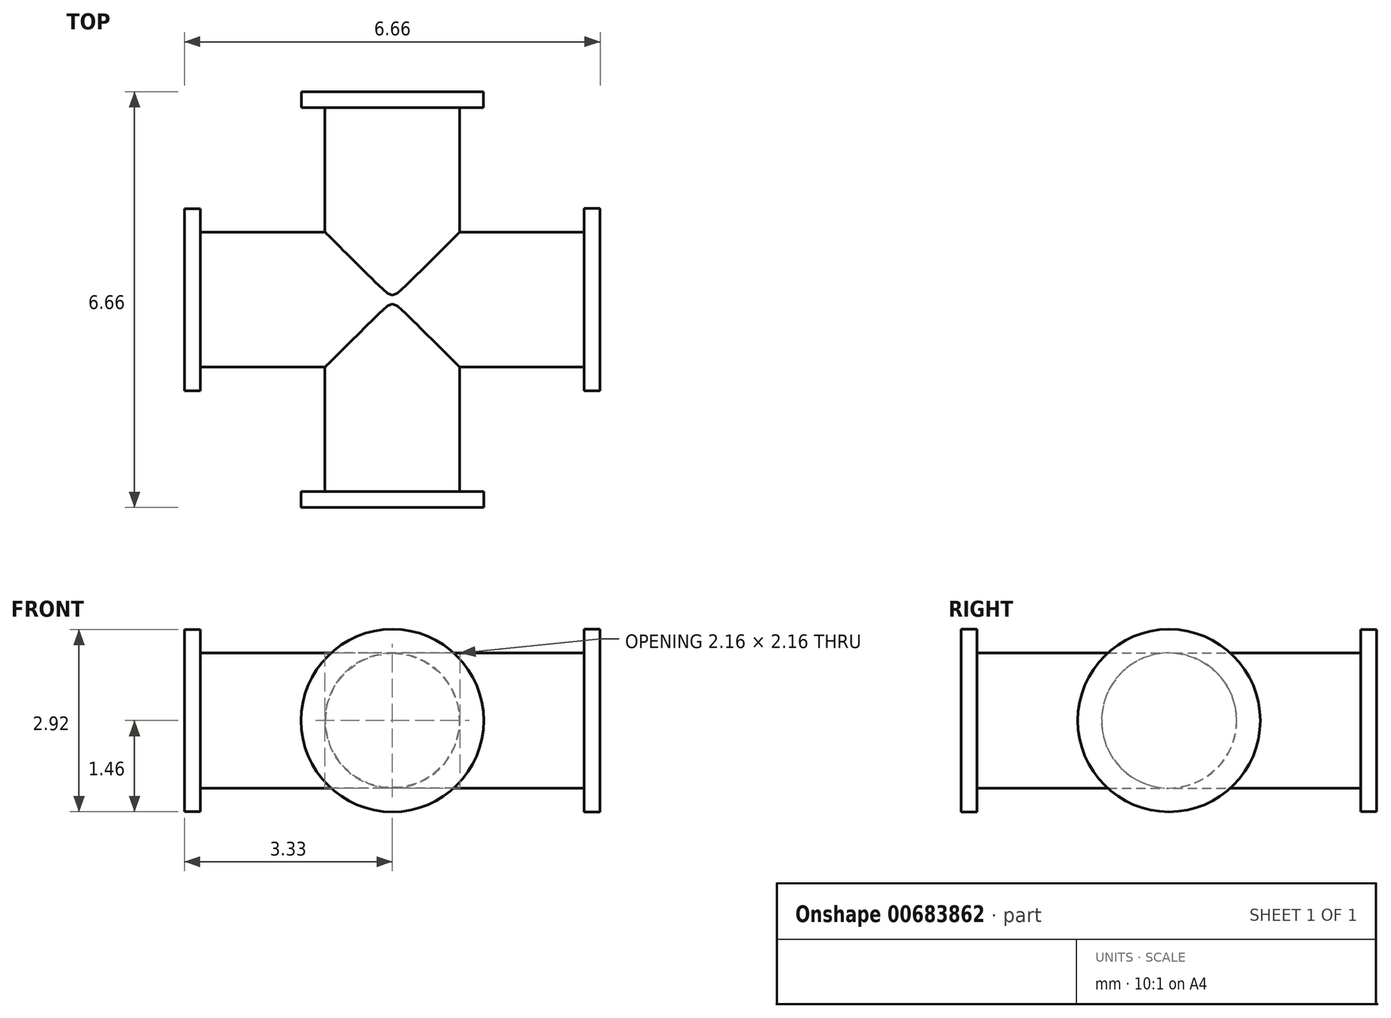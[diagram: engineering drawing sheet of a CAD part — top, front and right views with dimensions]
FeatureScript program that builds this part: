
annotation { "Feature Type Name" : "Feature", "Feature Type Description" : "" }
export const myFeature = defineFeature(function(context is Context, id is Id, definition is map)
    precondition{}
    {
        {
            var Q0;
            Q0=qCreatedBy(makeId("Front.planeOp"),FACE);
            var sketch = newSketch(context, id + "F0", { "sketchPlane" : qUnion([Q0])});
            skCircle(sketch, "E0", {"center": v(0, 0) * mm, "radius": 1.08 * mm});
            skSolve(sketch);
        }
        {
            var Q0;
            Q0=makeQuery(id+"F0.imprint","IMPRINT",FACE,{"disambiguationData":[TD([[makeQuery(id+"F0.imprint","IMPRINT",EDGE,{"derivedFrom":sQuery(id+"F0.wireOp",EDGE,"E0")}),1.0]])]});
            extrude(context, id + "F1", {"entities" : qUnion([Q0]), "depth" : 3.07 * mm, "offsetDistance" : 25.4 * mm, "hasSecondDirection" : true, "secondDirectionOppositeDirection" : true, "secondDirectionDepth" : 3.07 * mm});
        }
        {
            var Q0;
            Q0=qCreatedBy(makeId("Right.planeOp"),FACE);
            var sketch = newSketch(context, id + "F2", { "sketchPlane" : qUnion([Q0])});
            skCircle(sketch, "E1", {"center": v(0, 0) * mm, "radius": 1.08 * mm});
            skSolve(sketch);
        }
        {
            var Q0;
            Q0 = qSketchRegion(id + "F2", true);
            extrude(context, id + "F3", {"entities" : qUnion([Q0]), "operationType" : NewBodyOperationType.ADD, "depth" : 3.07 * mm, "offsetDistance" : 25.4 * mm, "hasSecondDirection" : true, "secondDirectionOppositeDirection" : true, "secondDirectionDepth" : 3.07 * mm});
        }
        {
            var Q0;
            Q0=makeQuery(id+"F1.opExtrude","CAP_FACE",FACE,{"disambiguationData":[OSD([sQuery(id+"F0.wireOp",EDGE,"E0")])],"isStart":false});
            var sketch = newSketch(context, id + "F4", { "sketchPlane" : qUnion([Q0])});
            skCircle(sketch, "E2", {"center": v(0, 0) * mm, "radius": 1.46 * mm});
            skSolve(sketch);
        }
        {
            var Q0;
            Q0 = qSketchRegion(id + "F4", true);
            extrude(context, id + "F5", {"entities" : qUnion([Q0]), "operationType" : NewBodyOperationType.ADD, "depth" : 0.25 * mm, "offsetDistance" : 25.4 * mm});
        }
        {
            var Q0;
            Q0=makeQuery(id+"F3.opExtrude","CAP_FACE",FACE,{"disambiguationData":[OSD([sQuery(id+"F2.wireOp",EDGE,"E1")])],"isStart":false});
            var sketch = newSketch(context, id + "F6", { "sketchPlane" : qUnion([Q0])});
            skCircle(sketch, "E3", {"center": v(0, 0) * mm, "radius": 1.46 * mm});
            skSolve(sketch);
        }
        {
            var Q0;
            Q0 = qSketchRegion(id + "F6", true);
            extrude(context, id + "F7", {"entities" : qUnion([Q0]), "operationType" : NewBodyOperationType.ADD, "depth" : 0.25 * mm, "offsetDistance" : 25.4 * mm});
        }
        {
            var Q0;
            Q0=makeQuery(id+"F1.opExtrude","CAP_FACE",FACE,{"disambiguationData":[OSD([sQuery(id+"F0.wireOp",EDGE,"E0")])],"isStart":true});
            var sketch = newSketch(context, id + "F8", { "sketchPlane" : qUnion([Q0])});
            skCircle(sketch, "E4", {"center": v(0, 0) * mm, "radius": 1.46 * mm});
            skSolve(sketch);
        }
        {
            var Q0;
            Q0 = qSketchRegion(id + "F8", true);
            extrude(context, id + "F9", {"entities" : qUnion([Q0]), "operationType" : NewBodyOperationType.ADD, "depth" : 0.25 * mm, "offsetDistance" : 25.4 * mm});
        }
        {
            var Q0;
            Q0=makeQuery(id+"F3.opExtrude","CAP_FACE",FACE,{"disambiguationData":[OSD([sQuery(id+"F2.wireOp",EDGE,"E1")])],"isStart":true});
            var sketch = newSketch(context, id + "F10", { "sketchPlane" : qUnion([Q0])});
            skCircle(sketch, "E5", {"center": v(0, 0) * mm, "radius": 1.46 * mm});
            skSolve(sketch);
        }
        {
            var Q0;
            Q0 = qSketchRegion(id + "F10", true);
            extrude(context, id + "F11", {"entities" : qUnion([Q0]), "operationType" : NewBodyOperationType.ADD, "depth" : 0.25 * mm, "offsetDistance" : 25.4 * mm});
        }
    });
